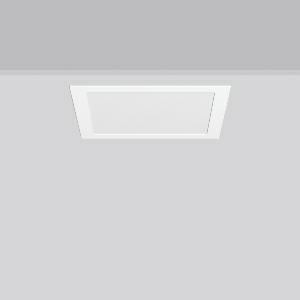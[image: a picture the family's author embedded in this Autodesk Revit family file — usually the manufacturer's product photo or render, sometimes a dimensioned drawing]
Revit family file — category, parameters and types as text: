
# Revit family: toledo_flat_square_e_672239_002_ce44
name_source: partatom
category: Lighting Fixtures
units: mm (PartAtom-declared; Revit-internal decimal feet)

## family parameters
Cut with Voids When Loaded = No
Host = Face
Light Source = No
Part Type = Normal
Room Calculation Point = No
Round Connector Dimension = Use Diameter
Shared = No

## types (1)
- TOLEDO FLAT square E (1 x LED Modul 830, 2050 lm, 3000)
    Apparent Load = 25 VA
    CIE Flux Codes = 48 80 96 100 100
    Color Rendering = 80
    Color Temperature = 3000
    Default Elevation = 1800 mm
    Description = Series: TOLEDO FLAT square
Square recessed downlight. For escape route illumination. Housing: die-cast aluminium, powder-coated. Lightguide and diffuser made of non-yellowing plastic (PMMA). Diffuser opal matt plastic. Ceiling installation with spring system. Including separate LED converter with connecting cable 250 mm. Self-contained system with automatic self-test. External driver with simple plug-in locking system. 
Colour: white
Length: 300 mm
Width: 300 mm
Height: 3 mm
Cut-out length: 280 mm
Cut-out width: 280 mm
Recess height: 90 mm
Luminaire: recess height: 60-80 mm
Weight: 2.23 kg
Operating mode: maintained power mode
Duration time: 3 h
Lamp: LED
Socket: without socket
Colour temperature: 3000K
Colour rendering index (CRI): 80
System power: 25 W
Rated luminous flux: 2050 lm
Luminous flux, emergency: 420 lm
System power, emergency: -
Control gear: Regulated power supply
Protection class: I
Type of protection: IP 54
    Height = 0 mm  [stored 0 ft]
    Lamp = 1 x LED Modul 830
    Lamp Light Flux = 2050 lm
    Lamp count = 1
    Length = 300 mm
    Lifetime = 50000 h
    Luminous efficacy = 82 lm/W
    Manufacturer = RZB
    ModVariant = No
    Model = 672239.002
    Mounting Place = Ceiling
    Mounting Type = Recessed
    Number of Poles = 1
    OnlyDefault = Yes
    Power Factor = 1
    Product Name = TOLEDO FLAT square E
    Product group = Recessed downlights
    ProductGroupID = 402
    Protection Class = Protection class I
    Protection Degree = IP 40
    RLX_Detail_Level = 1
    RLX_Emergency_Light_Flux = 420 lm
    RLX_Emergency_Type = 3
    RLX_Emergency_Type_DB = Yes
    RlxData = <blob elided: 13201 chars, md5=43406b4a>
    Socket = socket
    Standby Power = 0 W
    System Light Flux = 2050 lm
    System Power = 25 W
    Type Comments = Product without accessories
    Type Image = 901488.002.jpg
    URL = http://relux.com
    VarID = ---
    Voltage = 0 V
    Weight = 0.00 kg
    Width = 300 mm

note: [stored X ft] marks values corroborated as IEEE doubles in the binary element streams (Revit-internal decimal feet)

## geometry (parser evidence)
native form markers: Sweep x9
no freeform markers — native parametric forms only
